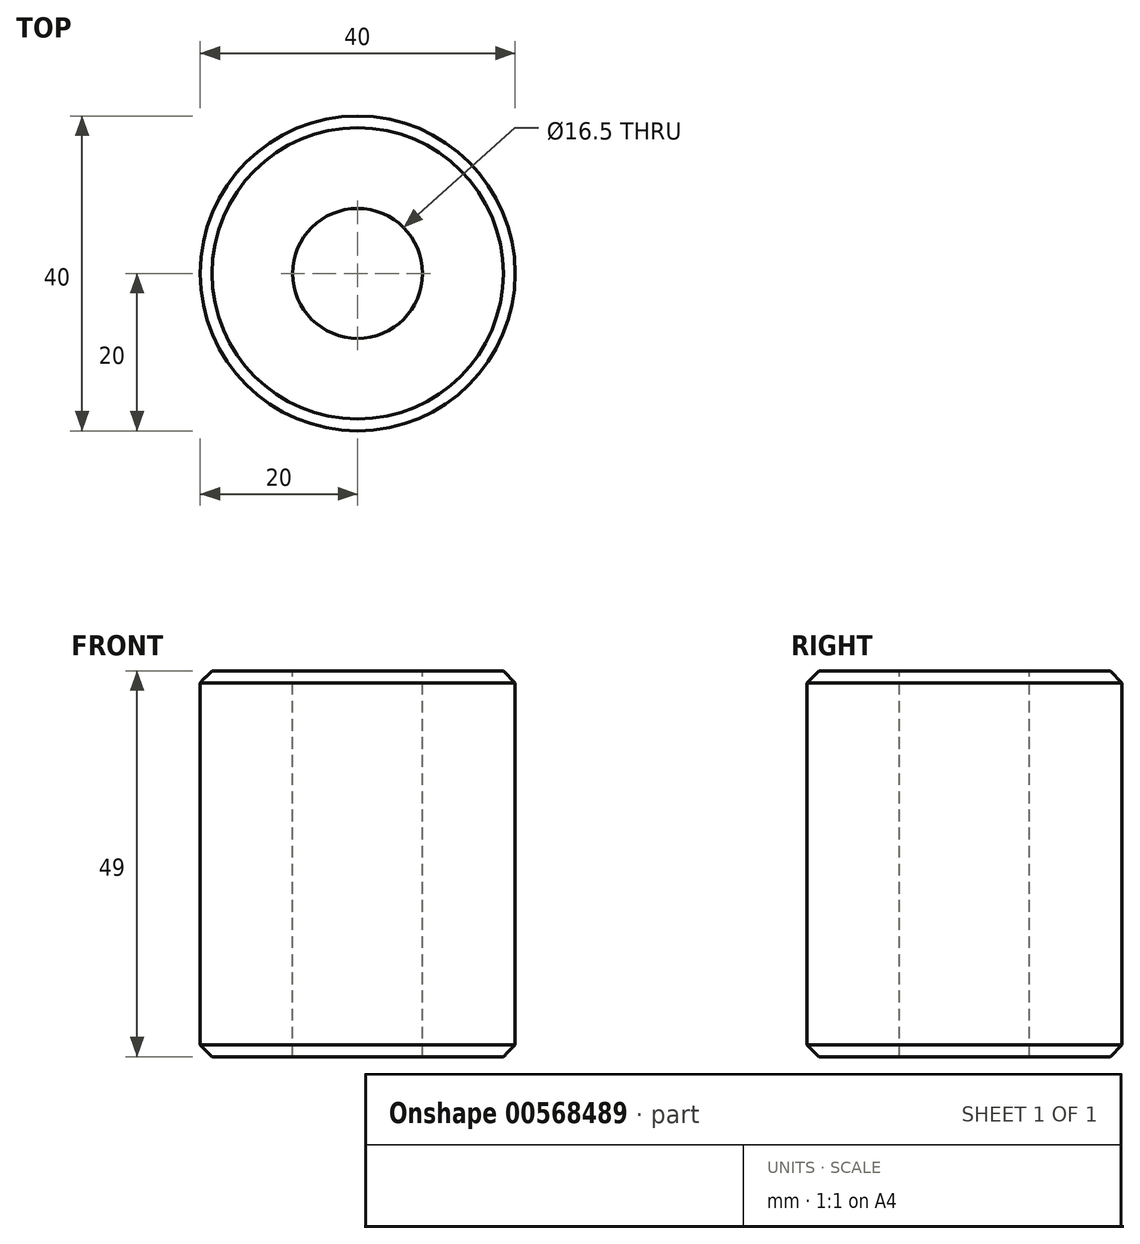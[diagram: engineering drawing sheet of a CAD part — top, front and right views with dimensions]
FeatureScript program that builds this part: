
annotation { "Feature Type Name" : "Feature", "Feature Type Description" : "" }
export const myFeature = defineFeature(function(context is Context, id is Id, definition is map)
    precondition{}
    {
        {
            var Q0;
            Q0=qCreatedBy(makeId("Front.planeOp"),FACE);
            var sketch = newSketch(context, id + "F0", { "sketchPlane" : qUnion([Q0])});
            skLineSegment(sketch, "E0", {"start": v(0, 0) * mm, "end": v(0, 43.81) * mm, "construction": true});
            skLineSegment(sketch, "E1", {"start": v(0, 49) * mm, "end": v(20, 49) * mm});
            skLineSegment(sketch, "E2", {"start": v(20, 49) * mm, "end": v(20, 0) * mm});
            skLineSegment(sketch, "E3", {"start": v(20, 0) * mm, "end": v(0, 0) * mm});
            skLineSegment(sketch, "E4", {"start": v(0, 49) * mm, "end": v(0, 0) * mm});
            skSolve(sketch);
        }
        {
            var Q0;
            Q0=makeQuery(id+"F0.imprint","IMPRINT",FACE,{"disambiguationData":[TD([[makeQuery(id+"F0.imprint","IMPRINT",EDGE,{"derivedFrom":sQuery(id+"F0.wireOp",EDGE,"E1")}),-1.0]])]});
            var Q1;
            Q1=sQuery(id+"F0.wireOp",EDGE,"E0");
            revolve(context, id + "F1", {"entities" : qUnion([Q0]), "axis" : qUnion([Q1]), "revolveType" : RevolveType.FULL});
        }
        {
            var Q0;
            Q0=makeQuery(id+"F1.opRevolve","SWEPT_FACE",FACE,{"disambiguationData":[OSD([sQuery(id+"F0.wireOp",EDGE,"E1")])]});
            var sketch = newSketch(context, id + "F2", { "sketchPlane" : qUnion([Q0])});
            skPoint(sketch, "E5", {"position": v(0, 0) * mm});
            skSolve(sketch);
        }
        {
            var Q0;
            Q0=sQuery(id+"F2.wireOp",VERTEX,"E5");
            var Q1;
            Q1=makeQuery(id+"F1.opRevolve","SWEPT_BODY",BODY,{"disambiguationData":[OSD([sQuery(id+"F0.wireOp",EDGE,"E1"),sQuery(id+"F0.wireOp",EDGE,"E2"),sQuery(id+"F0.wireOp",EDGE,"E3"),sQuery(id+"F0.wireOp",EDGE,"E4")])]});
            hole(context, id + "F3", {"style" : HoleStyle.SIMPLE, "endStyle" : HoleEndStyle.THROUGH, "holeDiameter" : 16.5 * mm, "isTappedThrough" : true, "tappedDepth" : 12 * mm, "tapClearance" : 3, "locations" : qUnion([Q0]), "scope" : qUnion([Q1])});
        }
        {
            var Q0;
            Q0=makeQuery(id+"F1.opRevolve","SWEPT_EDGE",EDGE,{"disambiguationData":[OSD([sQuery(id+"F0.wireOp",EDGE,"E1"),sQuery(id+"F0.wireOp",EDGE,"E2")])]});
            var Q1;
            Q1=makeQuery(id+"F1.opRevolve","SWEPT_EDGE",EDGE,{"disambiguationData":[OSD([sQuery(id+"F0.wireOp",EDGE,"E2"),sQuery(id+"F0.wireOp",EDGE,"E3")])]});
            chamfer(context, id + "F4", {"entities" : qUnion([Q0, Q1]), "width" : 1.5 * mm, "tangentPropagation" : true});
        }
    });
